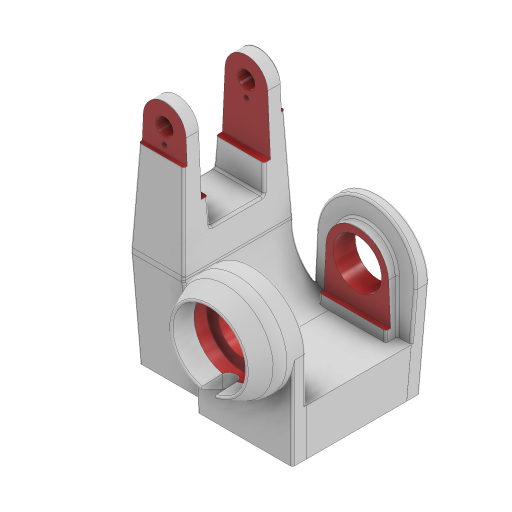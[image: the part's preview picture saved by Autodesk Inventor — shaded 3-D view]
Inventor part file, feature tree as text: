
AUTODESK INVENTOR PART (.ipt)
format: ipt  version: 2023 (Build 270158000, 158)  size: 1,138,688 bytes
history: native  units: mm
features: sketch x22, extrude x19, other x11, fillet x8, projected_geometry x5, mirror x4, hole x4
ambient origin geometry x8: Origin, YZ Plane, XZ Plane, XY Plane, X Axis, Y Axis, Z Axis, Center Point
bodies: Solide1 (feature_tree)
feature tree (73):
  sketch  "Esquisse1"
  extrude  "Extrusion1"  Depth=152.0mm
  extrude  "Extrusion2"  Depth=30.0mm
  mirror  "Symétrie1"
  other  "Plan de construction1"
  extrude  "Extrusion3"  Depth=71.0mm
  other  "Plan de construction2"
  extrude  "Extrusion4"  Depth=18.75mm
  mirror  "Symétrie2"
  other  "Plan de construction3"
  sketch  "Esquisse6"
  other  "Plan de construction4"
  extrude  "Extrusion5"  Depth=37.5mm
  extrude  "Extrusion6"  Depth=69.5mm
  mirror  "Symétrie3"
  extrude  "Extrusion7"  Depth=70.0mm
  extrude  "Extrusion8"  Depth=52.0mm
  extrude  "Extrusion9"  Depth=30.0mm
  extrude  "Extrusion10"  Depth=0.46067mm
  mirror  "Symétrie4"
  other  "PLAN DE JOINT"
  other  "Révolution1"
  extrude  "Extrusion11"  Depth=0.460767mm
  fillet  "Congé1"  Radius=0.460767mm
  other  "Plan de construction6"
  sketch  "Esquisse14"
  extrude  "Extrusion12"  Depth=36.3mm
  extrude  "Extrusion13"  Depth=50.0mm
  sketch  "Esquisse15"
  extrude  "Extrusion14"  Depth=77.0mm TaperAngle=0.0deg
  extrude  "Extrusion15"  Depth=0.467748mm
  fillet  "Congé2"  Radius=11.7mm
  other  "Dépouille de face2"
  fillet  "Congé3"  Radius=34.0mm
  fillet  "Congé4"  Radius=74.0mm
  fillet  "Congé5"  Radius=0.467748mm
  fillet  "Congé6"  [1 undecoded]
  fillet  "Congé7"  Radius=9.5mm
  fillet  "Congé9"  Radius=7.39mm
  other  "FIN DU BRUT ======"
  extrude  "Extrusion16"  Depth=35.0mm
  sketch  "Esquisse19"
  hole  "Perçage1"  [1 undecoded]
  hole  "Perçage2"  [1 undecoded]
  extrude  "Extrusion17"  Depth=0.467748mm
  other  "Plan de construction7"
  extrude  "Extrusion18"  Depth=70.0mm TaperAngle=0.0deg
  hole  "Perçage3"  [1 undecoded]
  other  "Plan de construction8"
  extrude  "Extrusion19"  Depth=0.453786mm
  hole  "Perçage4"  [1 undecoded]
  sketch  "Esquisse2"
  sketch  "Esquisse3"
  sketch  "Esquisse4"
  sketch  "Esquisse5"
  projected_geometry  "Boucle projetée1"
  sketch  "Esquisse7"
  projected_geometry  "Boucle projetée2"
  sketch  "Esquisse8"
  sketch  "Esquisse9"
  sketch  "Esquisse10"
  sketch  "Esquisse11"
  projected_geometry  "Boucle projetée3"
  sketch  "Esquisse12"
  projected_geometry  "Boucle projetée4"
  sketch  "Esquisse13"
  projected_geometry  "Boucle projetée5"
  sketch  "Esquisse18"
  sketch  "Esquisse20"
  sketch  "Esquisse21"
  sketch  "Esquisse22"
  sketch  "Esquisse23"
  sketch  "Esquisse24"
note: 5 required parameter values undecoded (feature->parameter linkage not recoverable at this tier; creation-order binding heuristic only, values carry confidence <= 0.55)
